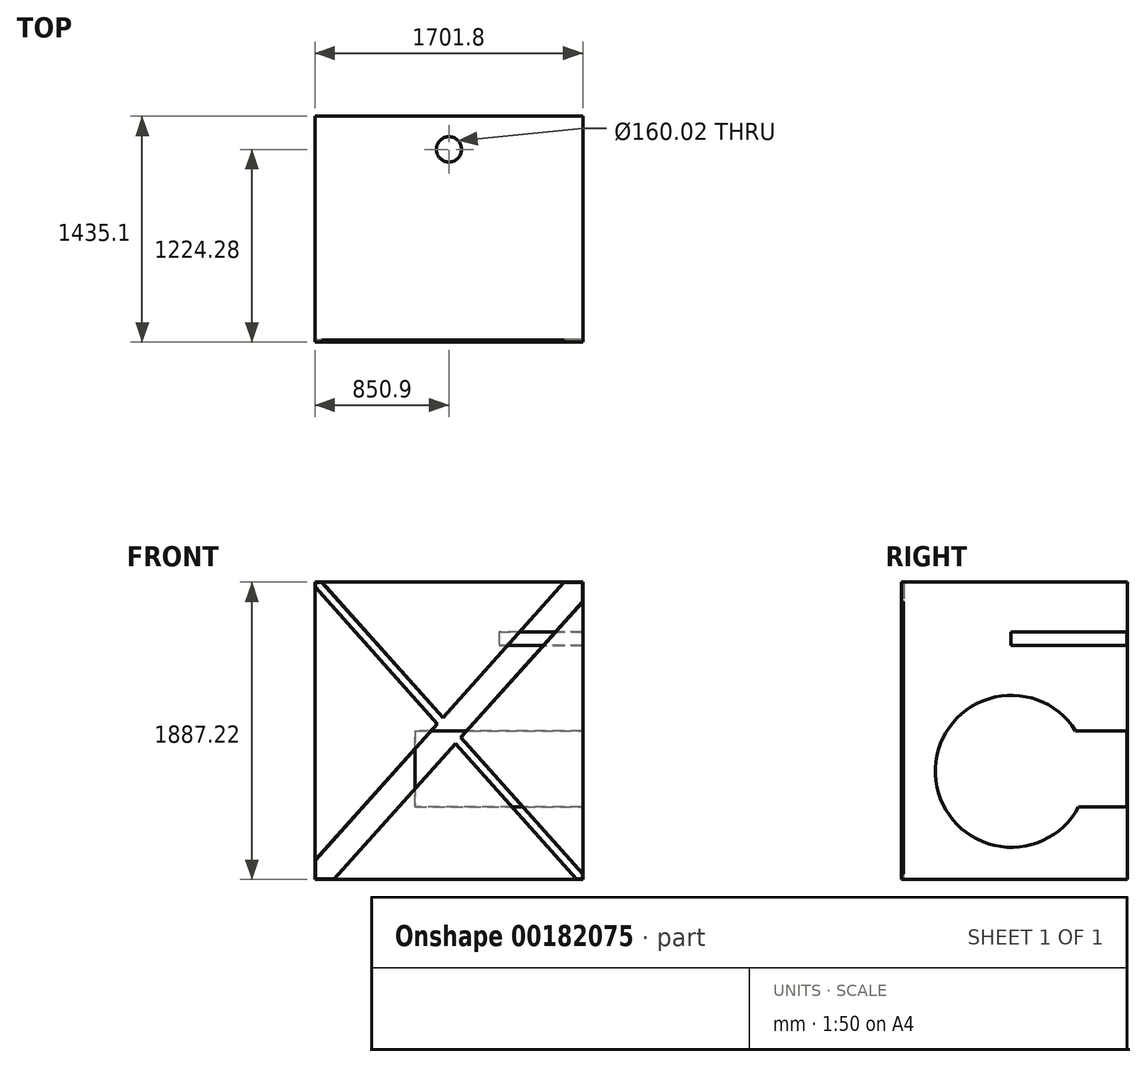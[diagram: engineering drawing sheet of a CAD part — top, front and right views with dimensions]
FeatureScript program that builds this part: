
annotation { "Feature Type Name" : "Feature", "Feature Type Description" : "" }
export const myFeature = defineFeature(function(context is Context, id is Id, definition is map)
    precondition{}
    {
        {
            var Q0;
            Q0=qCreatedBy(makeId("Front.planeOp"),FACE);
            var sketch = newSketch(context, id + "F0", { "sketchPlane" : qUnion([Q0])});
            skLineSegment(sketch, "E0.bottom", {"start": v(850.9, 943.6) * mm, "end": v(-850.9, 943.6) * mm});
            skLineSegment(sketch, "E0.top", {"start": v(850.9, -943.61) * mm, "end": v(-850.9, -943.61) * mm});
            skLineSegment(sketch, "E0.left", {"start": v(850.9, 943.6) * mm, "end": v(850.9, -943.61) * mm});
            skLineSegment(sketch, "E0.right", {"start": v(-850.9, 943.61) * mm, "end": v(-850.9, -943.6) * mm});
            skPoint(sketch, "E0.middle", {"position": v(0, 0) * mm});
            skSolve(sketch);
        }
        {
            var Q0;
            Q0 = qSketchRegion(id + "F0", true);
            extrude(context, id + "F1", {"entities" : qUnion([Q0]), "endBound" : BoundingType.SYMMETRIC, "depth" : 1422.4 * mm});
        }
        {
            var Q0;
            Q0=makeQuery(id+"F1.opExtrude","CAP_FACE",FACE,{"disambiguationData":[OSD([sQuery(id+"F0.wireOp",EDGE,"E0.bottom"),sQuery(id+"F0.wireOp",EDGE,"E0.top"),sQuery(id+"F0.wireOp",EDGE,"E0.left"),sQuery(id+"F0.wireOp",EDGE,"E0.right")])],"isStart":false});
            var sketch = newSketch(context, id + "F2", { "sketchPlane" : qUnion([Q0])});
            skPoint(sketch, "E1", {"position": v(-850.9, -821.7) * mm});
            skPoint(sketch, "E2", {"position": v(-729.28, -943.61) * mm});
            skPoint(sketch, "E3", {"position": v(-850.9, -943.6) * mm});
            skPoint(sketch, "E4", {"position": v(731.36, 943.6) * mm});
            skPoint(sketch, "E5", {"position": v(850.9, 819.65) * mm});
            skLineSegment(sketch, "E6", {"start": v(850.9, 819.65) * mm, "end": v(-729.28, -943.61) * mm});
            skLineSegment(sketch, "E7", {"start": v(731.36, 943.6) * mm, "end": v(-850.9, -821.7) * mm});
            skPoint(sketch, "E8", {"position": v(-850.9, 913.15) * mm});
            skPoint(sketch, "E9", {"position": v(-806.5, 943.6) * mm});
            skPoint(sketch, "E10", {"position": v(850.9, -908.12) * mm});
            skPoint(sketch, "E11", {"position": v(810.4, -943.61) * mm});
            skPoint(sketch, "E12", {"position": v(-74.1, 44.96) * mm});
            skPoint(sketch, "E13", {"position": v(77.2, -43.7) * mm});
            skPoint(sketch, "E14", {"position": v(41.18, -83.89) * mm});
            skPoint(sketch, "E15", {"position": v(-38.1, 85.13) * mm});
            skLineSegment(sketch, "E16", {"start": v(-38.1, 85.13) * mm, "end": v(-806.5, 943.6) * mm});
            skLineSegment(sketch, "E17", {"start": v(-74.1, 44.96) * mm, "end": v(-850.9, 913.15) * mm});
            skLineSegment(sketch, "E18", {"start": v(77.2, -43.7) * mm, "end": v(850.9, -908.12) * mm});
            skLineSegment(sketch, "E19", {"start": v(41.18, -83.89) * mm, "end": v(810.4, -943.6) * mm});
            skSolve(sketch);
        }
        {
            var Q0;
            Q0=makeQuery(id+"F1.opExtrude","SWEPT_FACE",FACE,{"disambiguationData":[OSD([sQuery(id+"F0.wireOp",EDGE,"E0.left")])]});
            var sketch = newSketch(context, id + "F3", { "sketchPlane" : qUnion([Q0])});
            skPoint(sketch, "E20", {"position": v(-25.4, -257.8) * mm});
            skCircle(sketch, "E21", {"center": v(-25.4, -257.8) * mm, "radius": 482.6 * mm});
            skPoint(sketch, "E22", {"position": v(711.2, 0) * mm});
            skPoint(sketch, "E23", {"position": v(711.2, -482.6) * mm});
            skLineSegment(sketch, "E24", {"start": v(711.2, 0) * mm, "end": v(382.57, 0) * mm});
            skLineSegment(sketch, "E25", {"start": v(711.2, -482.6) * mm, "end": v(401.65, -482.6) * mm});
            skSolve(sketch);
        }
        {
            var Q0;
            {var subQ4=sQuery(id+"F2.wireOp",EDGE,"E6");var subQ12=makeQuery(id+"F1.opExtrude","CAP_EDGE",EDGE,{"disambiguationData":[OSD([sQuery(id+"F0.wireOp",EDGE,"E0.left")])],"isStart":false});var subQ13=makeQuery(id+"F2.imprint","INTERSECT",VERTEX,{"derivedFrom":[subQ12,subQ4]});Q0=makeQuery(id+"F2.imprint","IMPRINT",FACE,{"disambiguationData":[TD([[makeQuery(id+"F2.imprint","IMPRINT",EDGE,{"disambiguationData":[TD([[subQ13,-1.0]])],"derivedFrom":subQ4}),-1.0]])]});}
            var Q1;
            {var subQ3=sQuery(id+"F2.wireOp",EDGE,"E16");Q1=makeQuery(id+"F2.imprint","IMPRINT",FACE,{"disambiguationData":[TD([[makeQuery(id+"F2.imprint","IMPRINT",EDGE,{"derivedFrom":subQ3}),1.0]])]});}
            var Q2;
            {var subQ4=sQuery(id+"F2.wireOp",EDGE,"E18");Q2=makeQuery(id+"F2.imprint","IMPRINT",FACE,{"disambiguationData":[TD([[makeQuery(id+"F2.imprint","IMPRINT",EDGE,{"derivedFrom":subQ4}),-1.0]])]});}
            extrude(context, id + "F4", {"entities" : qUnion([Q0, Q1, Q2]), "operationType" : NewBodyOperationType.ADD, "endBound" : BoundingType.SYMMETRIC, "depth" : 25.4 * mm});
        }
        {
            var Q0;
            Q0=makeQuery(id+"F4.opExtrude","CAP_FACE",FACE,{"disambiguationData":[OSD([sQuery(id+"F0.wireOp",EDGE,"E0.bottom"),sQuery(id+"F0.wireOp",EDGE,"E0.top"),sQuery(id+"F0.wireOp",EDGE,"E0.left"),sQuery(id+"F0.wireOp",EDGE,"E0.right"),sQuery(id+"F2.wireOp",EDGE,"E6"),sQuery(id+"F2.wireOp",EDGE,"E7"),sQuery(id+"F2.wireOp",EDGE,"E16"),sQuery(id+"F2.wireOp",EDGE,"E17"),sQuery(id+"F2.wireOp",EDGE,"E18"),sQuery(id+"F2.wireOp",EDGE,"E19")])],"isStart":false});
            shell(context, id + "F5", {"entities" : qUnion([Q0]), "thickness" : 2.54 * mm});
        }
        {
            var Q0;
            {var subQ4=sQuery(id+"F3.wireOp",EDGE,"E24");Q0=makeQuery(id+"F3.imprint","IMPRINT",FACE,{"disambiguationData":[TD([[makeQuery(id+"F3.imprint","IMPRINT",EDGE,{"derivedFrom":subQ4}),-1.0]])]});}
            var sketch = newSketch(context, id + "F6", { "sketchPlane" : qUnion([Q0])});
            skPoint(sketch, "E26", {"position": v(709.2, 626.12) * mm});
            skLineSegment(sketch, "E27.bottom", {"start": v(709.2, 626.12) * mm, "end": v(-27.4, 626.12) * mm});
            skLineSegment(sketch, "E27.top", {"start": v(709.2, 542.3) * mm, "end": v(-27.4, 542.3) * mm});
            skLineSegment(sketch, "E27.left", {"start": v(709.2, 626.12) * mm, "end": v(709.2, 542.3) * mm});
            skLineSegment(sketch, "E27.right", {"start": v(-27.4, 626.12) * mm, "end": v(-27.4, 542.3) * mm});
            skSolve(sketch);
        }
        {
            var Q0;
            Q0=makeQuery(id+"F6.imprint","IMPRINT",FACE,{"disambiguationData":[TD([[makeQuery(id+"F6.imprint","IMPRINT",EDGE,{"derivedFrom":sQuery(id+"F6.wireOp",EDGE,"E27.bottom")}),1.0]])]});
            extrude(context, id + "F7", {"entities" : qUnion([Q0]), "operationType" : NewBodyOperationType.REMOVE, "endBound" : BoundingType.SYMMETRIC, "oppositeDirection" : true, "depth" : 1066.8 * mm});
        }
        {
            var Q0;
            {var subQ0=sQuery(id+"F3.wireOp",EDGE,"E21");var subQ1=makeQuery(id+"F3.imprint","INTERSECT",VERTEX,{"derivedFrom":[subQ0,sQuery(id+"F3.wireOp",EDGE,"E24")]});Q0=makeQuery(id+"F3.imprint","IMPRINT",FACE,{"disambiguationData":[TD([[makeQuery(id+"F3.imprint","IMPRINT",EDGE,{"disambiguationData":[TD([[subQ1,-1.0]])],"derivedFrom":subQ0}),1.0]])]});}
            var Q1;
            {var subQ0=sQuery(id+"F3.wireOp",EDGE,"E24");Q1=makeQuery(id+"F3.imprint","IMPRINT",FACE,{"disambiguationData":[TD([[makeQuery(id+"F3.imprint","IMPRINT",EDGE,{"derivedFrom":subQ0}),1.0]])]});}
            extrude(context, id + "F8", {"entities" : qUnion([Q0, Q1]), "operationType" : NewBodyOperationType.REMOVE, "endBound" : BoundingType.SYMMETRIC, "oppositeDirection" : true, "depth" : 2133.6 * mm});
        }
        {
            var Q0;
            {var subQ0=sQuery(id+"F0.wireOp",EDGE,"E0.bottom");var subQ1=makeQuery(id+"F1.opExtrude","CAP_EDGE",EDGE,{"disambiguationData":[OSD([subQ0])],"isStart":false});Q0=makeQuery(id+"F4.boolean.opBoolean","MERGE",FACE,{"derivedFrom":[makeQuery(id+"F1.opExtrude","SWEPT_FACE",FACE,{"disambiguationData":[OSD([subQ0])]}),makeQuery(id+"F4.opExtrude","SWEPT_FACE",FACE,{"disambiguationData":[OSD([subQ0]),TDD([makeQuery(id+"F2.imprint","IMPRINT",EDGE,{"disambiguationData":[TD([[makeQuery(id+"F2.imprint","INTERSECT",VERTEX,{"derivedFrom":[subQ1,makeQuery(id+"F1.opExtrude","CAP_EDGE",EDGE,{"disambiguationData":[OSD([sQuery(id+"F0.wireOp",EDGE,"E0.left")])],"isStart":false})]}),-1.0]])],"derivedFrom":subQ1})])]}),makeQuery(id+"F4.opExtrude","SWEPT_FACE",FACE,{"disambiguationData":[OSD([subQ0]),TDD([makeQuery(id+"F2.imprint","IMPRINT",EDGE,{"disambiguationData":[TD([[makeQuery(id+"F2.imprint","INTERSECT",VERTEX,{"derivedFrom":[subQ1,makeQuery(id+"F1.opExtrude","CAP_EDGE",EDGE,{"disambiguationData":[OSD([sQuery(id+"F0.wireOp",EDGE,"E0.right")])],"isStart":false})]}),1.0]])],"derivedFrom":subQ1})])]})]});}
            var sketch = newSketch(context, id + "F9", { "sketchPlane" : qUnion([Q0])});
            skPoint(sketch, "E28", {"position": v(0, 500.38) * mm});
            skCircle(sketch, "E29", {"center": v(0, 500.38) * mm, "radius": 80.01 * mm});
            skSolve(sketch);
        }
        {
            var Q0;
            Q0 = qSketchRegion(id + "F9", true);
            extrude(context, id + "F10", {"entities" : qUnion([Q0]), "operationType" : NewBodyOperationType.REMOVE, "endBound" : BoundingType.SYMMETRIC, "oppositeDirection" : true, "depth" : 609.6 * mm});
        }
        {
            var Q0;
            Q0=makeQuery(id+"F7.boolean.opBoolean","COPY",FACE,{"derivedFrom":makeQuery(id+"F7.opExtrude","SWEPT_FACE",FACE,{"disambiguationData":[OSD([sQuery(id+"F6.wireOp",EDGE,"E27.left")])]})});
            extrude(context, id + "F11", {"entities" : qUnion([Q0]), "operationType" : NewBodyOperationType.REMOVE, "oppositeDirection" : true, "depth" : 1066.8 * mm});
        }
    });
